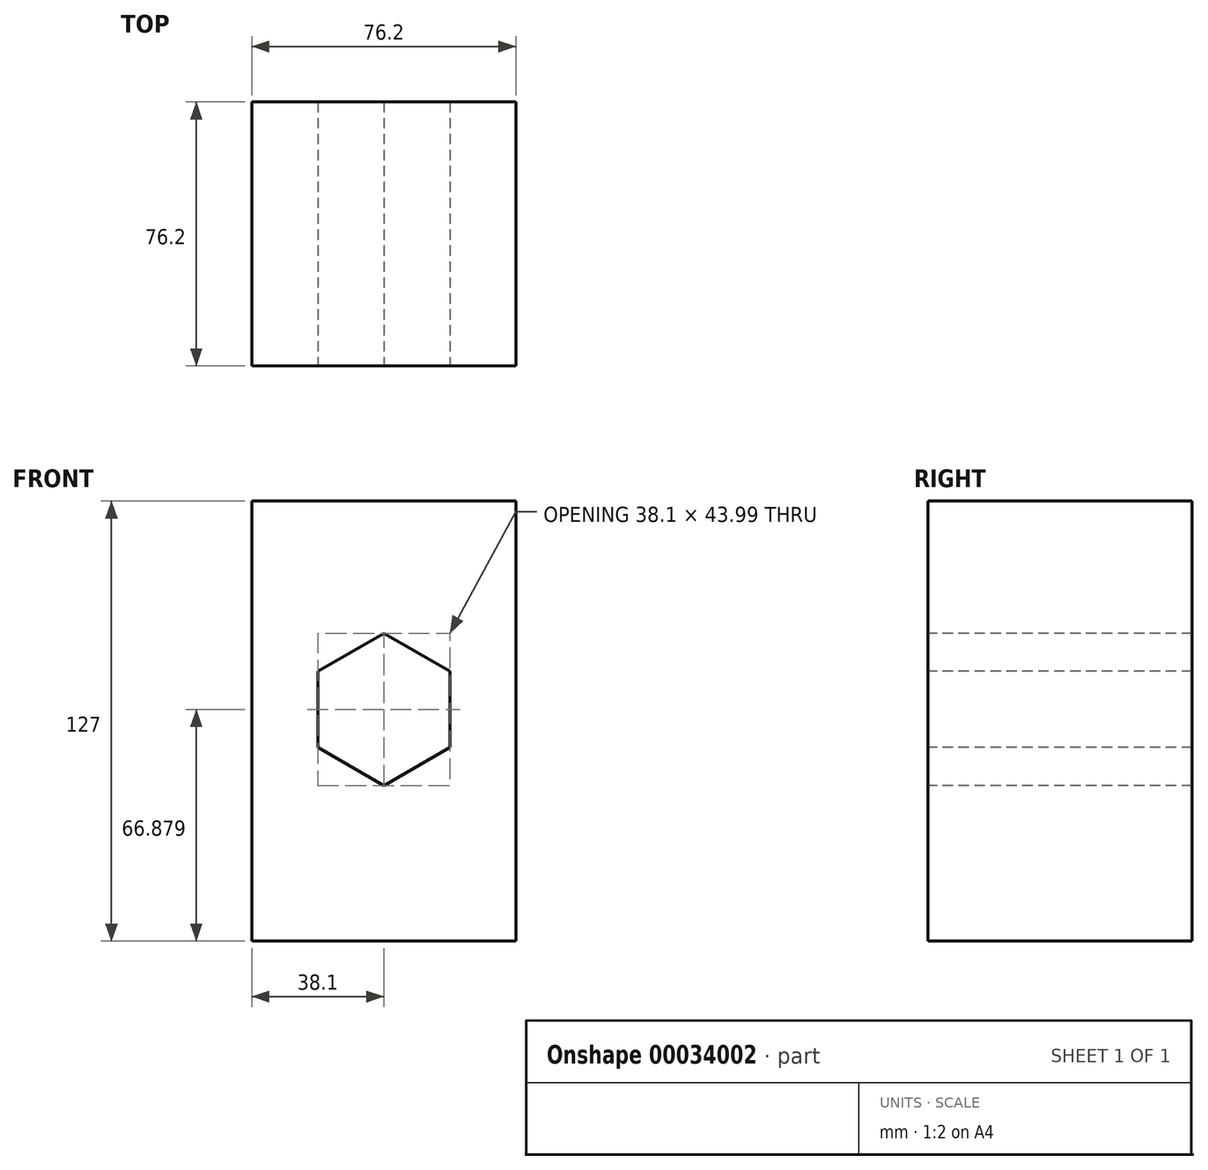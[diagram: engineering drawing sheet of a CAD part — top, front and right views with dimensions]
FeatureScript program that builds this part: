
annotation { "Feature Type Name" : "Feature", "Feature Type Description" : "" }
export const myFeature = defineFeature(function(context is Context, id is Id, definition is map)
    precondition{}
    {
        {
            var Q0;
            Q0=qCreatedBy(makeId("Front.planeOp"),FACE);
            var sketch = newSketch(context, id + "F0", { "sketchPlane" : qUnion([Q0])});
            skLineSegment(sketch, "E0.bottom", {"start": v(0, 0) * mm, "end": v(76.2, 0) * mm});
            skLineSegment(sketch, "E0.top", {"start": v(0, 127) * mm, "end": v(76.2, 127) * mm});
            skLineSegment(sketch, "E0.left", {"start": v(0, 0) * mm, "end": v(0, 127) * mm});
            skLineSegment(sketch, "E0.right", {"start": v(76.2, 0) * mm, "end": v(76.2, 127) * mm});
            skSolve(sketch);
        }
        {
            var Q0;
            Q0 = qSketchRegion(id + "F0", true);
            extrude(context, id + "F1", {"entities" : qUnion([Q0]), "oppositeDirection" : true, "depth" : 76.2 * mm});
        }
        {
            var Q0;
            Q0=makeQuery(id+"F0.imprint","IMPRINT",FACE,{"disambiguationData":[TD([[makeQuery(id+"F0.imprint","IMPRINT",EDGE,{"derivedFrom":sQuery(id+"F0.wireOp",EDGE,"E0.bottom")}),1.0]])]});
            var sketch = newSketch(context, id + "F2", { "sketchPlane" : qUnion([Q0])});
            skCircle(sketch, "E1.cCircle", {"center": v(38.1, 66.88) * mm, "radius": 19.05 * mm, "construction": true});
            skLineSegment(sketch, "E1.0", {"start": v(57.15, 77.88) * mm, "end": v(57.15, 55.88) * mm});
            skLineSegment(sketch, "E1.1", {"start": v(57.15, 55.88) * mm, "end": v(38.1, 44.88) * mm});
            skLineSegment(sketch, "E1.2", {"start": v(38.1, 44.88) * mm, "end": v(19.05, 55.88) * mm});
            skLineSegment(sketch, "E1.3", {"start": v(19.05, 55.88) * mm, "end": v(19.05, 77.88) * mm});
            skLineSegment(sketch, "E1.4", {"start": v(19.05, 77.88) * mm, "end": v(38.1, 88.88) * mm});
            skLineSegment(sketch, "E1.5", {"start": v(38.1, 88.88) * mm, "end": v(57.15, 77.88) * mm});
            skPoint(sketch, "E1.0.midPoint", {"position": v(57.15, 66.88) * mm});
            skSolve(sketch);
        }
        {
            var Q0;
            Q0 = qSketchRegion(id + "F2", true);
            extrude(context, id + "F3", {"entities" : qUnion([Q0]), "operationType" : NewBodyOperationType.REMOVE, "endBound" : BoundingType.THROUGH_ALL, "oppositeDirection" : true, "depth" : 25.4 * mm});
        }
    });
